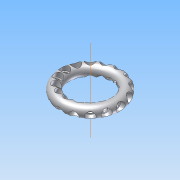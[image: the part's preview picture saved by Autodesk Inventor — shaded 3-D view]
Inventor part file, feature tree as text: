
AUTODESK INVENTOR PART (.ipt)
format: ipt  version: 2012 (Build 160160000, 160)  size: 636,416 bytes
history: native  units: mm
features: other x35, extrude x32, plane x2, sketch x1
ambient origin geometry x8: Origin, YZ Plane, XZ Plane, XY Plane, X Axis, Y Axis, Z Axis, Center Point
feature tree (70):
  other  "basic-frame"
  other  "plane-0"
  other  "circle-0"
  other  "plane-1"
  other  "circle-1"
  other  "plane-2"
  other  "circle-2"
  other  "plane-3"
  other  "circle-3"
  other  "plane-4"
  other  "circle-4"
  other  "plane-5"
  other  "circle-5"
  other  "plane-6"
  other  "circle-6"
  other  "plane-7"
  other  "circle-7"
  other  "plane-8"
  other  "circle-8"
  other  "plane-9"
  other  "circle-9"
  other  "plane-10"
  other  "circle-10"
  other  "plane-11"
  other  "circle-11"
  other  "plane-12"
  other  "circle-12"
  other  "plane-13"
  other  "circle-13"
  other  "plane-14"
  other  "circle-14"
  other  "plane-15"
  other  "circle-15"
  plane  "工作平面17"
  plane  "工作平面18"
  other  "tire"
  extrude  "hole0"  TaperAngle=0.0deg  [1 undecoded]
  extrude  "support0"  Depth=1.963495mm
  extrude  "hole1"  TaperAngle=22.5deg  [1 undecoded]
  extrude  "support1"  Depth=5.890486mm
  extrude  "hole2"  TaperAngle=45.0deg  [1 undecoded]
  extrude  "support2"  Depth=9.817477mm
  extrude  "hole3"  TaperAngle=67.5deg  [1 undecoded]
  extrude  "support3"  Depth=13.744468mm
  extrude  "hole4"  TaperAngle=90.0deg  [1 undecoded]
  extrude  "support4"  Depth=17.671459mm
  extrude  "hole5"  TaperAngle=112.5deg  [1 undecoded]
  extrude  "support5"  Depth=21.598449mm
  extrude  "hole6"  TaperAngle=135.0deg  [1 undecoded]
  extrude  "support6"  Depth=25.52544mm
  extrude  "hole7"  TaperAngle=157.5deg  [1 undecoded]
  extrude  "support7"  Depth=29.452431mm
  extrude  "hole8"  Depth=10.0mm
  extrude  "support8"  Depth=15.2mm
  extrude  "hole9"  Depth=15.2mm
  extrude  "support9"  Depth=10.0mm
  extrude  "hole10"  Depth=15.2mm
  extrude  "support10"  Depth=10.0mm
  extrude  "hole11"  Depth=10.0mm
  extrude  "support11"  Depth=15.2mm
  extrude  "hole12"  Depth=15.2mm
  extrude  "support12"  Depth=10.0mm
  extrude  "hole13"  Depth=15.2mm
  extrude  "support13"  Depth=10.0mm
  extrude  "hole14"  Depth=15.2mm
  extrude  "support14"  Depth=10.0mm
  extrude  "hole15"  Depth=15.2mm
  extrude  "support15"  Depth=10.0mm
  other  "工作轴1"
  sketch  "草图22"  dims[d1=90.727207mm d13=0.0mm d14=1.963495mm d15=22.5deg d16=5.890486mm d17=45.0deg d18=9.817477mm d19=67.5deg d20=13.744468mm d21=90.0deg d22=17.671459mm d23=112.5deg d24=21.598449mm d25=135.0deg d26=25.52544mm d27=157.5deg d28=29.452431mm d76=10.0mm d77=15.2mm d78=15.2mm d79=10.0mm d80=15.2mm d81=10.0mm d82=10.0mm d83=15.2mm d84=15.2mm d85=10.0mm d86=15.2mm d87=10.0mm d88=15.2mm d89=10.0mm d90=15.2mm d91=10.0mm d92=15.2mm d93=10.0mm d94=15.2mm d95=10.0mm d96=15.2mm d97=10.0mm d98=15.2mm d99=10.0mm d100=15.2mm d101=10.0mm d102=15.2mm d103=10.0mm d104=15.2mm d105=10.0mm d106=15.2mm d107=160.0mm d109=360.0deg d115=17.7mm d116=0.0mm d118=0.0mm d119=2.0mm d120=0.0mm d121=2.0mm d122=0.0mm d123=2.0mm d124=0.0mm d125=2.0mm d126=0.0mm d127=2.0mm d128=0.0mm d129=2.0mm d130=0.0mm d131=2.0mm d132=0.0mm d133=2.0mm d134=0.0mm d135=2.0mm d136=0.0mm d137=2.0mm d138=0.0mm d139=2.0mm d140=0.0mm d141=2.0mm d142=0.0mm d143=2.0mm d144=0.0mm d145=2.0mm d146=0.0mm d147=2.0mm d148=0.0mm d149=2.0mm d150=0.0mm d151=35.4mm d152=0.0mm d153=2.0mm d154=0.0mm d155=2.0mm d156=0.0mm d157=2.0mm d158=0.0mm d159=2.0mm d160=0.0mm d161=2.0mm d162=0.0mm d163=2.0mm d164=0.0mm d165=2.0mm d166=0.0mm d167=90.0deg d168=2.0mm d169=0.0mm d170=2.0mm d171=0.0mm d172=2.0mm d173=0.0mm d174=2.0mm d175=0.0mm d176=2.0mm d177=0.0mm d178=2.0mm d179=0.0mm]
note: 8 required parameter values undecoded (feature->parameter linkage not recoverable at this tier; creation-order binding heuristic only, values carry confidence <= 0.55)
